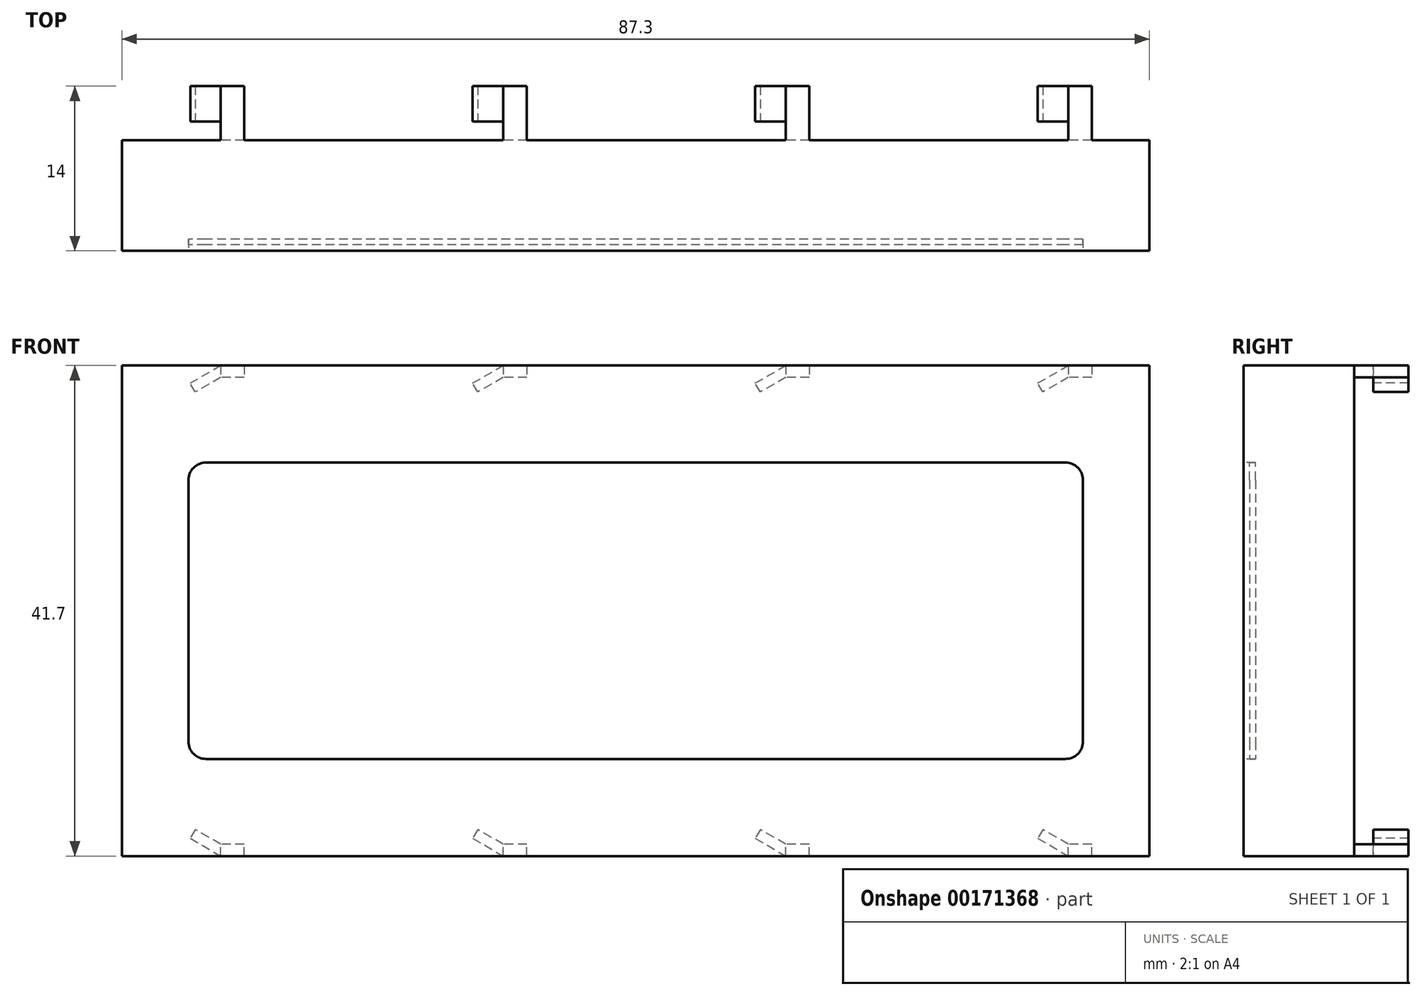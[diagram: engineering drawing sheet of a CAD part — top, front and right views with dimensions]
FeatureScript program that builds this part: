
annotation { "Feature Type Name" : "Feature", "Feature Type Description" : "" }
export const myFeature = defineFeature(function(context is Context, id is Id, definition is map)
    precondition{}
    {
        {
            var Q0;
            Q0=qCreatedBy(makeId("Front.planeOp"),FACE);
            var sketch = newSketch(context, id + "F0", { "sketchPlane" : qUnion([Q0])});
            skLineSegment(sketch, "E0.bottom", {"start": v(43.65, 20.85) * mm, "end": v(-43.65, 20.85) * mm});
            skLineSegment(sketch, "E0.top", {"start": v(43.65, -20.85) * mm, "end": v(-43.65, -20.85) * mm});
            skLineSegment(sketch, "E0.left", {"start": v(43.65, 20.85) * mm, "end": v(43.65, -20.85) * mm});
            skLineSegment(sketch, "E0.right", {"start": v(-43.65, 20.85) * mm, "end": v(-43.65, -20.85) * mm});
            skPoint(sketch, "E0.middle", {"position": v(0, 0) * mm});
            skSolve(sketch);
        }
        {
            var Q0;
            Q0 = qSketchRegion(id + "F0", true);
            extrude(context, id + "F1", {"entities" : qUnion([Q0]), "depth" : 9.4 * mm});
        }
        {
            var Q0;
            Q0=makeQuery(id+"F1.opExtrude","CAP_FACE",FACE,{"disambiguationData":[OSD([sQuery(id+"F0.wireOp",EDGE,"E0.bottom"),sQuery(id+"F0.wireOp",EDGE,"E0.top"),sQuery(id+"F0.wireOp",EDGE,"E0.left"),sQuery(id+"F0.wireOp",EDGE,"E0.right")])],"isStart":false});
            var sketch = newSketch(context, id + "F2", { "sketchPlane" : qUnion([Q0])});
            skLineSegment(sketch, "E1.bottom", {"start": v(36.5, 12.6) * mm, "end": v(-36.5, 12.6) * mm});
            skLineSegment(sketch, "E1.top", {"start": v(36.5, -12.6) * mm, "end": v(-36.5, -12.6) * mm});
            skLineSegment(sketch, "E1.left", {"start": v(38, 11.1) * mm, "end": v(38, -11.1) * mm});
            skLineSegment(sketch, "E1.right", {"start": v(-38, 11.1) * mm, "end": v(-38, -11.1) * mm});
            skPoint(sketch, "E1.middle", {"position": v(0, 0) * mm});
            skPoint(sketch, "E2.visualSharp", {"position": v(-38, 12.6) * mm});
            skArc(sketch, "E2.filletArc", {"start": v(-36.5, 12.6) * mm, "mid": v(-37.56, 12.16) * mm, "end": v(-38, 11.1) * mm});
            skPoint(sketch, "E3.visualSharp", {"position": v(38, 12.6) * mm});
            skArc(sketch, "E3.filletArc", {"start": v(38, 11.1) * mm, "mid": v(37.56, 12.16) * mm, "end": v(36.5, 12.6) * mm});
            skPoint(sketch, "E4.visualSharp", {"position": v(38, -12.6) * mm});
            skArc(sketch, "E4.filletArc", {"start": v(36.5, -12.6) * mm, "mid": v(37.56, -12.16) * mm, "end": v(38, -11.1) * mm});
            skPoint(sketch, "E5.visualSharp", {"position": v(-38, -12.6) * mm});
            skArc(sketch, "E5.filletArc", {"start": v(-38, -11.1) * mm, "mid": v(-37.56, -12.16) * mm, "end": v(-36.5, -12.6) * mm});
            skSolve(sketch);
        }
        {
            var Q0;
            Q0 = qSketchRegion(id + "F2", true);
            extrude(context, id + "F3", {"entities" : qUnion([Q0]), "operationType" : NewBodyOperationType.REMOVE, "oppositeDirection" : true, "depth" : 1 * mm});
        }
        {
            var Q0;
            Q0=makeQuery(id+"F3.boolean.opBoolean","COPY",FACE,{"derivedFrom":makeQuery(id+"F3.opExtrude","CAP_FACE",FACE,{"disambiguationData":[OSD([sQuery(id+"F2.wireOp",EDGE,"E1.bottom"),sQuery(id+"F2.wireOp",EDGE,"E1.top"),sQuery(id+"F2.wireOp",EDGE,"E1.left"),sQuery(id+"F2.wireOp",EDGE,"E1.right"),sQuery(id+"F2.wireOp",EDGE,"E2.filletArc"),sQuery(id+"F2.wireOp",EDGE,"E3.filletArc"),sQuery(id+"F2.wireOp",EDGE,"E4.filletArc"),sQuery(id+"F2.wireOp",EDGE,"E5.filletArc")])],"isStart":false})});
            var sketch = newSketch(context, id + "F4", { "sketchPlane" : qUnion([Q0])});
            skLineSegment(sketch, "E6.0", {"start": v(-38, 11.1) * mm, "end": v(-38, -11.1) * mm});
            skArc(sketch, "E7.0", {"start": v(-38, -11.1) * mm, "mid": v(-37.56, -12.16) * mm, "end": v(-36.5, -12.6) * mm});
            skLineSegment(sketch, "E7.1", {"start": v(36.5, -12.6) * mm, "end": v(-36.5, -12.6) * mm});
            skArc(sketch, "E7.2", {"start": v(36.5, -12.6) * mm, "mid": v(37.56, -12.16) * mm, "end": v(38, -11.1) * mm});
            skLineSegment(sketch, "E7.3", {"start": v(38, 11.1) * mm, "end": v(38, -11.1) * mm});
            skArc(sketch, "E7.4", {"start": v(38, 11.1) * mm, "mid": v(37.56, 12.16) * mm, "end": v(36.5, 12.6) * mm});
            skLineSegment(sketch, "E7.5", {"start": v(36.5, 12.6) * mm, "end": v(-36.5, 12.6) * mm});
            skArc(sketch, "E7.6", {"start": v(-36.5, 12.6) * mm, "mid": v(-37.56, 12.16) * mm, "end": v(-38, 11.1) * mm});
            skSolve(sketch);
        }
        {
            var Q0;
            Q0 = qSketchRegion(id + "F4", true);
            extrude(context, id + "F5", {"entities" : qUnion([Q0]), "depth" : 0.5 * mm});
        }
        {
            var Q0;
            Q0=makeQuery(id+"F1.opExtrude","CAP_FACE",FACE,{"disambiguationData":[OSD([sQuery(id+"F0.wireOp",EDGE,"E0.bottom"),sQuery(id+"F0.wireOp",EDGE,"E0.top"),sQuery(id+"F0.wireOp",EDGE,"E0.left"),sQuery(id+"F0.wireOp",EDGE,"E0.right")])],"isStart":true});
            var sketch = newSketch(context, id + "F6", { "sketchPlane" : qUnion([Q0])});
            skLineSegment(sketch, "E8.bottom", {"start": v(9.25, 20.85) * mm, "end": v(11.25, 20.85) * mm});
            skLineSegment(sketch, "E8.top", {"start": v(9.25, 19.85) * mm, "end": v(11.25, 19.85) * mm});
            skLineSegment(sketch, "E8.left", {"start": v(9.25, 20.85) * mm, "end": v(9.25, 19.85) * mm});
            skLineSegment(sketch, "E8.right", {"start": v(11.25, 20.85) * mm, "end": v(11.25, 19.85) * mm});
            skLineSegment(sketch, "E9.bottom", {"start": v(33.26, 20.85) * mm, "end": v(35.26, 20.85) * mm});
            skLineSegment(sketch, "E9.top", {"start": v(33.26, 19.85) * mm, "end": v(35.26, 19.85) * mm});
            skLineSegment(sketch, "E9.left", {"start": v(33.26, 20.85) * mm, "end": v(33.26, 19.85) * mm});
            skLineSegment(sketch, "E9.right", {"start": v(35.26, 20.85) * mm, "end": v(35.26, 19.85) * mm});
            skLineSegment(sketch, "E10.bottom", {"start": v(-38.75, 20.85) * mm, "end": v(-36.75, 20.85) * mm});
            skLineSegment(sketch, "E10.top", {"start": v(-38.75, 19.85) * mm, "end": v(-36.75, 19.85) * mm});
            skLineSegment(sketch, "E10.left", {"start": v(-38.75, 20.85) * mm, "end": v(-38.75, 19.85) * mm});
            skLineSegment(sketch, "E10.right", {"start": v(-36.75, 20.85) * mm, "end": v(-36.75, 19.85) * mm});
            skLineSegment(sketch, "E11.bottom", {"start": v(-14.75, 20.85) * mm, "end": v(-12.75, 20.85) * mm});
            skLineSegment(sketch, "E11.top", {"start": v(-14.75, 19.85) * mm, "end": v(-12.75, 19.85) * mm});
            skLineSegment(sketch, "E11.left", {"start": v(-14.75, 20.85) * mm, "end": v(-14.75, 19.85) * mm});
            skLineSegment(sketch, "E11.right", {"start": v(-12.75, 20.85) * mm, "end": v(-12.75, 19.85) * mm});
            skLineSegment(sketch, "E12.MirrorCS", {"start": v(-14.75, -20.85) * mm, "end": v(-12.75, -20.85) * mm});
            skLineSegment(sketch, "E13.MirrorCS", {"start": v(-36.75, -20.85) * mm, "end": v(-36.75, -19.85) * mm});
            skLineSegment(sketch, "E14.MirrorCS", {"start": v(-38.75, -20.85) * mm, "end": v(-38.75, -19.85) * mm});
            skLineSegment(sketch, "E15.MirrorCS", {"start": v(-38.75, -19.85) * mm, "end": v(-36.75, -19.85) * mm});
            skLineSegment(sketch, "E16.MirrorCS", {"start": v(-38.75, -20.85) * mm, "end": v(-36.75, -20.85) * mm});
            skLineSegment(sketch, "E17.MirrorCS", {"start": v(33.26, -20.85) * mm, "end": v(33.26, -19.85) * mm});
            skLineSegment(sketch, "E18.MirrorCS", {"start": v(33.26, -19.85) * mm, "end": v(35.26, -19.85) * mm});
            skLineSegment(sketch, "E19.MirrorCS", {"start": v(33.26, -20.85) * mm, "end": v(35.26, -20.85) * mm});
            skLineSegment(sketch, "E20.MirrorCS", {"start": v(11.25, -20.85) * mm, "end": v(11.25, -19.85) * mm});
            skLineSegment(sketch, "E21.MirrorCS", {"start": v(35.26, -20.85) * mm, "end": v(35.26, -19.85) * mm});
            skLineSegment(sketch, "E22.MirrorCS", {"start": v(9.25, -20.85) * mm, "end": v(9.25, -19.85) * mm});
            skLineSegment(sketch, "E23.MirrorCS", {"start": v(-14.75, -19.85) * mm, "end": v(-12.75, -19.85) * mm});
            skLineSegment(sketch, "E24.MirrorCS", {"start": v(-14.75, -20.85) * mm, "end": v(-14.75, -19.85) * mm});
            skLineSegment(sketch, "E25.MirrorCS", {"start": v(-12.75, -20.85) * mm, "end": v(-12.75, -19.85) * mm});
            skLineSegment(sketch, "E26.MirrorCS", {"start": v(9.25, -20.85) * mm, "end": v(11.25, -20.85) * mm});
            skLineSegment(sketch, "E27.MirrorCS", {"start": v(9.25, -19.85) * mm, "end": v(11.25, -19.85) * mm});
            skSolve(sketch);
        }
        {
            var Q0;
            Q0 = qSketchRegion(id + "F6", true);
            extrude(context, id + "F7", {"entities" : qUnion([Q0]), "operationType" : NewBodyOperationType.ADD, "depth" : 1.6 * mm});
        }
        {
            var Q0;
            Q0=makeQuery(id+"F7.opExtrude","CAP_FACE",FACE,{"disambiguationData":[OSD([sQuery(id+"F6.wireOp",EDGE,"E10.bottom"),sQuery(id+"F6.wireOp",EDGE,"E10.top"),sQuery(id+"F6.wireOp",EDGE,"E10.left"),sQuery(id+"F6.wireOp",EDGE,"E10.right")])],"isStart":false});
            var sketch = newSketch(context, id + "F8", { "sketchPlane" : qUnion([Q0])});
            skLineSegment(sketch, "E28.0", {"start": v(-38.75, 20.85) * mm, "end": v(-38.75, 19.85) * mm});
            skLineSegment(sketch, "E28.1", {"start": v(-38.75, 20.85) * mm, "end": v(-36.75, 20.85) * mm});
            skLineSegment(sketch, "E28.2", {"start": v(-38.75, 19.85) * mm, "end": v(-36.75, 19.85) * mm});
            skLineSegment(sketch, "E29", {"start": v(-36.75, 19.85) * mm, "end": v(-34.58, 18.6) * mm});
            skLineSegment(sketch, "E30", {"start": v(-34.58, 18.6) * mm, "end": v(-34.15, 19.35) * mm});
            skLineSegment(sketch, "E31", {"start": v(-34.15, 19.35) * mm, "end": v(-36.75, 20.85) * mm});
            skLineSegment(sketch, "E32.1.0.0", {"start": v(-12.75, 19.85) * mm, "end": v(-10.58, 18.6) * mm});
            skLineSegment(sketch, "E32.1.0.1", {"start": v(-14.75, 19.85) * mm, "end": v(-12.75, 19.85) * mm});
            skLineSegment(sketch, "E32.1.0.2", {"start": v(-14.75, 20.85) * mm, "end": v(-14.75, 19.85) * mm});
            skLineSegment(sketch, "E32.1.0.3", {"start": v(-10.15, 19.35) * mm, "end": v(-12.75, 20.85) * mm});
            skLineSegment(sketch, "E32.1.0.4", {"start": v(-14.75, 20.85) * mm, "end": v(-12.75, 20.85) * mm});
            skLineSegment(sketch, "E32.1.0.5", {"start": v(-10.58, 18.6) * mm, "end": v(-10.15, 19.35) * mm});
            skLineSegment(sketch, "E32.2.0.0", {"start": v(11.25, 19.85) * mm, "end": v(13.42, 18.6) * mm});
            skLineSegment(sketch, "E32.2.0.1", {"start": v(9.25, 19.85) * mm, "end": v(11.25, 19.85) * mm});
            skLineSegment(sketch, "E32.2.0.2", {"start": v(9.25, 20.85) * mm, "end": v(9.25, 19.85) * mm});
            skLineSegment(sketch, "E32.2.0.3", {"start": v(13.85, 19.35) * mm, "end": v(11.25, 20.85) * mm});
            skLineSegment(sketch, "E32.2.0.4", {"start": v(9.25, 20.85) * mm, "end": v(11.25, 20.85) * mm});
            skLineSegment(sketch, "E32.2.0.5", {"start": v(13.42, 18.6) * mm, "end": v(13.85, 19.35) * mm});
            skLineSegment(sketch, "E32.3.0.0", {"start": v(35.25, 19.85) * mm, "end": v(37.42, 18.6) * mm});
            skLineSegment(sketch, "E32.3.0.1", {"start": v(33.25, 19.85) * mm, "end": v(35.25, 19.85) * mm});
            skLineSegment(sketch, "E32.3.0.2", {"start": v(33.25, 20.85) * mm, "end": v(33.25, 19.85) * mm});
            skLineSegment(sketch, "E32.3.0.3", {"start": v(37.85, 19.35) * mm, "end": v(35.25, 20.85) * mm});
            skLineSegment(sketch, "E32.3.0.4", {"start": v(33.25, 20.85) * mm, "end": v(35.25, 20.85) * mm});
            skLineSegment(sketch, "E32.3.0.5", {"start": v(37.42, 18.6) * mm, "end": v(37.85, 19.35) * mm});
            skLineSegment(sketch, "E32.direction1", {"start": v(-38.75, 19.85) * mm, "end": v(-14.75, 19.85) * mm, "construction": true});
            skLineSegment(sketch, "E33.MirrorCS", {"start": v(-38.75, -20.85) * mm, "end": v(-38.75, -19.85) * mm});
            skLineSegment(sketch, "E34.MirrorCS", {"start": v(-38.75, -19.85) * mm, "end": v(-36.75, -19.85) * mm});
            skLineSegment(sketch, "E35.MirrorCS", {"start": v(-14.75, -20.85) * mm, "end": v(-14.75, -19.85) * mm});
            skLineSegment(sketch, "E36.MirrorCS", {"start": v(9.25, -19.85) * mm, "end": v(11.25, -19.85) * mm});
            skLineSegment(sketch, "E37.MirrorCS", {"start": v(9.25, -20.85) * mm, "end": v(9.25, -19.85) * mm});
            skLineSegment(sketch, "E38.MirrorCS", {"start": v(13.85, -19.35) * mm, "end": v(11.25, -20.85) * mm});
            skLineSegment(sketch, "E39.MirrorCS", {"start": v(-38.75, -20.85) * mm, "end": v(-36.75, -20.85) * mm});
            skLineSegment(sketch, "E40.MirrorCS", {"start": v(35.25, -19.85) * mm, "end": v(37.42, -18.6) * mm});
            skLineSegment(sketch, "E41.MirrorCS", {"start": v(-36.75, -19.85) * mm, "end": v(-34.58, -18.6) * mm});
            skLineSegment(sketch, "E42.MirrorCS", {"start": v(-34.58, -18.6) * mm, "end": v(-34.15, -19.35) * mm});
            skLineSegment(sketch, "E43.MirrorCS", {"start": v(9.25, -20.85) * mm, "end": v(11.25, -20.85) * mm});
            skLineSegment(sketch, "E44.MirrorCS", {"start": v(-12.75, -19.85) * mm, "end": v(-10.58, -18.6) * mm});
            skLineSegment(sketch, "E45.MirrorCS", {"start": v(-14.75, -19.85) * mm, "end": v(-12.75, -19.85) * mm});
            skLineSegment(sketch, "E46.MirrorCS", {"start": v(-14.75, -20.85) * mm, "end": v(-12.75, -20.85) * mm});
            skLineSegment(sketch, "E47.MirrorCS", {"start": v(-10.58, -18.6) * mm, "end": v(-10.15, -19.35) * mm});
            skLineSegment(sketch, "E48.MirrorCS", {"start": v(11.25, -19.85) * mm, "end": v(13.42, -18.6) * mm});
            skLineSegment(sketch, "E49.MirrorCS", {"start": v(33.25, -20.85) * mm, "end": v(35.25, -20.85) * mm});
            skLineSegment(sketch, "E50.MirrorCS", {"start": v(33.25, -20.85) * mm, "end": v(33.25, -19.85) * mm});
            skLineSegment(sketch, "E51.MirrorCS", {"start": v(13.42, -18.6) * mm, "end": v(13.85, -19.35) * mm});
            skLineSegment(sketch, "E52.MirrorCS", {"start": v(33.25, -19.85) * mm, "end": v(35.25, -19.85) * mm});
            skLineSegment(sketch, "E53.MirrorCS", {"start": v(37.42, -18.6) * mm, "end": v(37.85, -19.35) * mm});
            skLineSegment(sketch, "E54.MirrorCS", {"start": v(-38.75, -19.85) * mm, "end": v(-14.75, -19.85) * mm, "construction": true});
            skLineSegment(sketch, "E55.MirrorCS", {"start": v(-34.15, -19.35) * mm, "end": v(-36.75, -20.85) * mm});
            skLineSegment(sketch, "E56.MirrorCS", {"start": v(-10.15, -19.35) * mm, "end": v(-12.75, -20.85) * mm});
            skLineSegment(sketch, "E57.MirrorCS", {"start": v(37.85, -19.35) * mm, "end": v(35.25, -20.85) * mm});
            skSolve(sketch);
        }
        {
            var Q0;
            Q0 = qSketchRegion(id + "F8", true);
            extrude(context, id + "F9", {"entities" : qUnion([Q0]), "operationType" : NewBodyOperationType.ADD, "depth" : 3 * mm});
        }
    });
